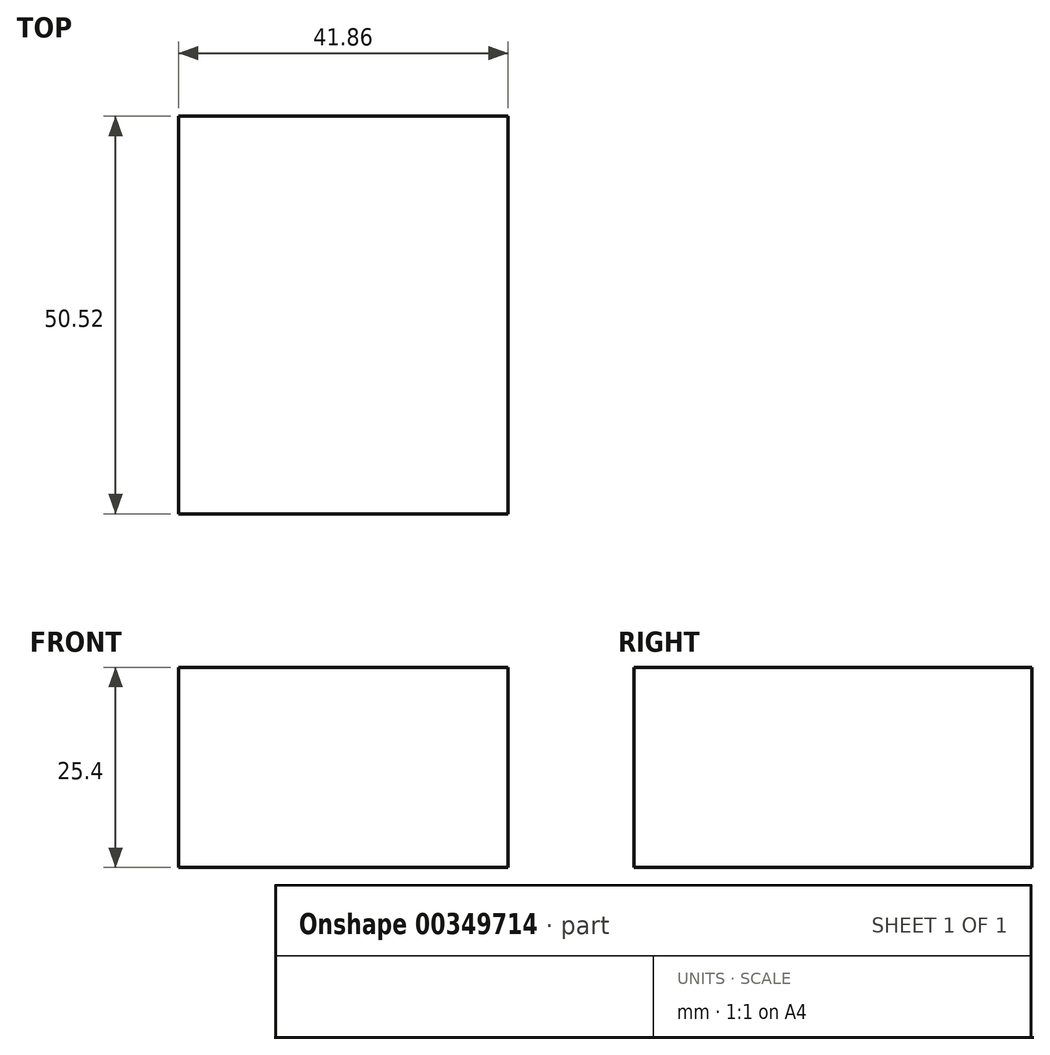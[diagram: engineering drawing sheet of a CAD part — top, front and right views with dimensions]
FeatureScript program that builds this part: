
annotation { "Feature Type Name" : "Feature", "Feature Type Description" : "" }
export const myFeature = defineFeature(function(context is Context, id is Id, definition is map)
    precondition{}
    {
        {
            var Q0;
            Q0=qCreatedBy(makeId("Top.planeOp"),FACE);
            var sketch = newSketch(context, id + "F0", { "sketchPlane" : qUnion([Q0])});
            skLineSegment(sketch, "E0.bottom", {"start": v(0, 0) * mm, "end": v(41.86, 0) * mm});
            skLineSegment(sketch, "E0.top", {"start": v(0, 50.52) * mm, "end": v(41.86, 50.52) * mm});
            skLineSegment(sketch, "E0.left", {"start": v(0, 0) * mm, "end": v(0, 50.52) * mm});
            skLineSegment(sketch, "E0.right", {"start": v(41.86, 0) * mm, "end": v(41.86, 50.52) * mm});
            skPoint(sketch, "E0.middle", {"position": v(20.93, 25.26) * mm});
            skSolve(sketch);
        }
        {
            var Q0;
            Q0=makeQuery(id+"F0.imprint","IMPRINT",FACE,{"disambiguationData":[TD([[makeQuery(id+"F0.imprint","IMPRINT",EDGE,{"derivedFrom":sQuery(id+"F0.wireOp",EDGE,"E0.bottom")}),1.0]])]});
            extrude(context, id + "F1", {"entities" : qUnion([Q0]), "depth" : 25.4 * mm});
        }
    });
